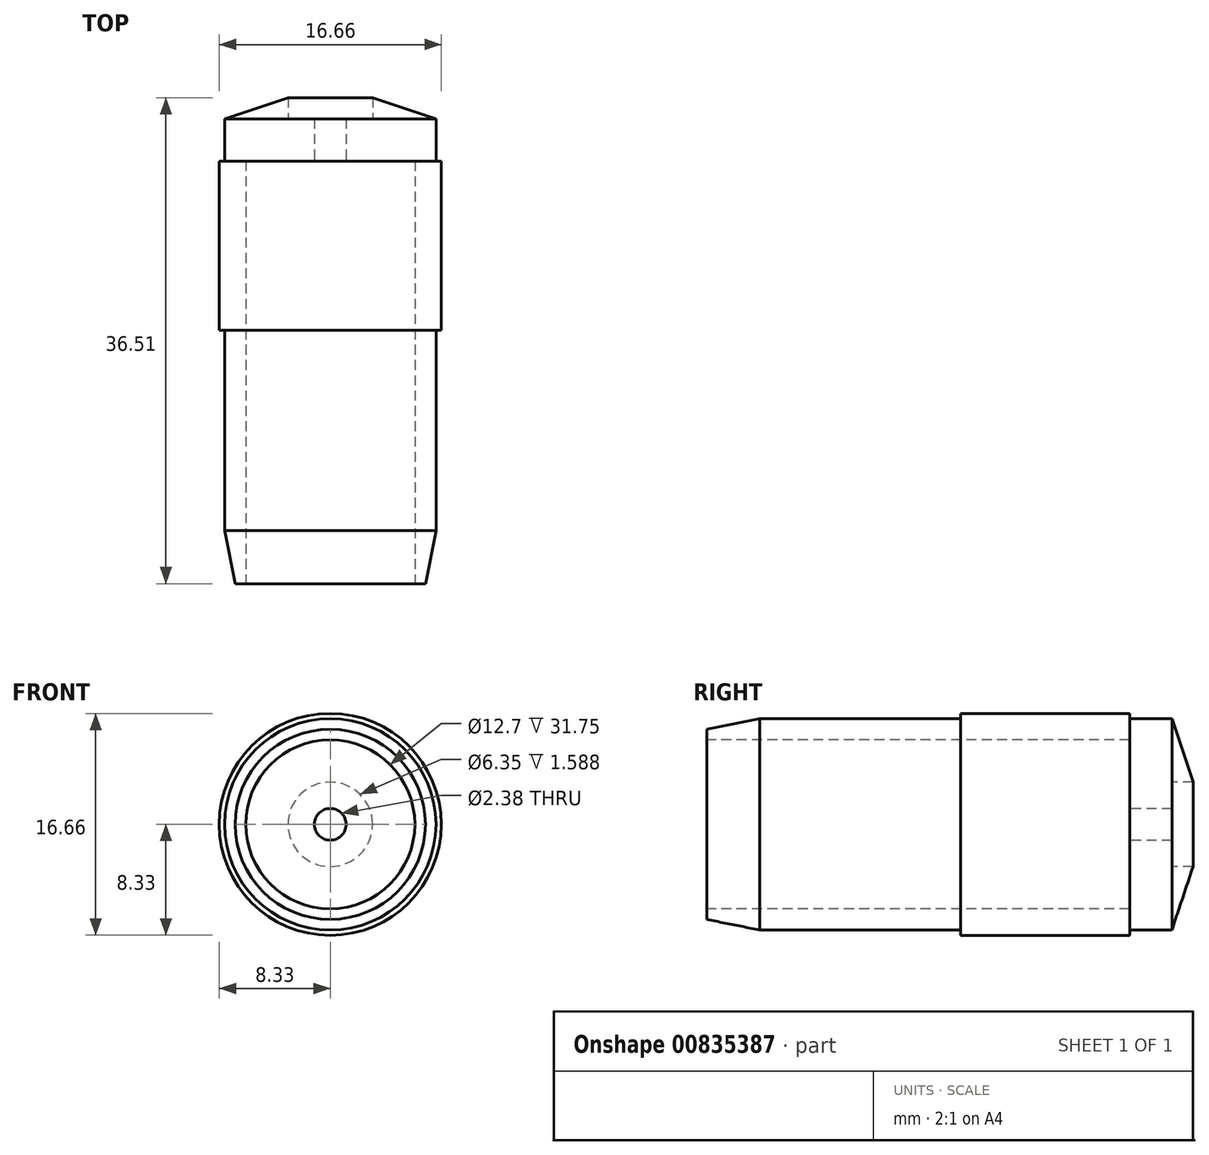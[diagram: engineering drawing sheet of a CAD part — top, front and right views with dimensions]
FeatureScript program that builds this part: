
annotation { "Feature Type Name" : "Feature", "Feature Type Description" : "" }
export const myFeature = defineFeature(function(context is Context, id is Id, definition is map)
    precondition{}
    {
        {
            var Q0;
            Q0=qCreatedBy(makeId("Top.planeOp"),FACE);
            var sketch = newSketch(context, id + "F0", { "sketchPlane" : qUnion([Q0])});
            skLineSegment(sketch, "E0", {"start": v(6.35, 0) * mm, "end": v(7.14, 0) * mm});
            skLineSegment(sketch, "E1", {"start": v(7.14, 0) * mm, "end": v(7.94, 4) * mm});
            skLineSegment(sketch, "E2", {"start": v(7.94, 4) * mm, "end": v(7.94, 19.05) * mm});
            skLineSegment(sketch, "E3", {"start": v(7.94, 19.05) * mm, "end": v(8.33, 19.05) * mm});
            skLineSegment(sketch, "E4", {"start": v(8.33, 19.05) * mm, "end": v(8.33, 31.75) * mm});
            skLineSegment(sketch, "E5", {"start": v(8.33, 31.75) * mm, "end": v(7.94, 31.75) * mm});
            skLineSegment(sketch, "E6", {"start": v(7.94, 31.75) * mm, "end": v(7.94, 34.93) * mm});
            skLineSegment(sketch, "E7", {"start": v(7.94, 34.93) * mm, "end": v(3.18, 36.51) * mm});
            skLineSegment(sketch, "E8", {"start": v(1.2, 31.75) * mm, "end": v(6.35, 31.75) * mm});
            skLineSegment(sketch, "E9", {"start": v(6.35, 31.75) * mm, "end": v(6.35, 0) * mm});
            skLineSegment(sketch, "E10", {"start": v(-6.35, 0) * mm, "end": v(-7.14, 0) * mm});
            skLineSegment(sketch, "E11", {"start": v(-7.14, 0) * mm, "end": v(-7.94, 4) * mm});
            skLineSegment(sketch, "E12", {"start": v(-7.94, 4) * mm, "end": v(-7.94, 19.05) * mm});
            skLineSegment(sketch, "E13", {"start": v(-7.94, 19.05) * mm, "end": v(-8.33, 19.05) * mm});
            skLineSegment(sketch, "E14", {"start": v(-8.33, 19.05) * mm, "end": v(-8.33, 31.75) * mm});
            skLineSegment(sketch, "E15", {"start": v(-8.33, 31.75) * mm, "end": v(-7.94, 31.75) * mm});
            skLineSegment(sketch, "E16", {"start": v(-7.94, 31.75) * mm, "end": v(-7.94, 34.93) * mm});
            skLineSegment(sketch, "E17", {"start": v(-7.94, 34.93) * mm, "end": v(-3.18, 36.51) * mm});
            skLineSegment(sketch, "E18", {"start": v(-1.2, 31.75) * mm, "end": v(-6.35, 31.75) * mm});
            skLineSegment(sketch, "E19", {"start": v(-6.35, 31.75) * mm, "end": v(-6.35, 0) * mm});
            skLineSegment(sketch, "E20", {"start": v(7.94, 4) * mm, "end": v(7.94, 0) * mm, "construction": true});
            skLineSegment(sketch, "E21", {"start": v(0, 0) * mm, "end": v(0, 36.51) * mm, "construction": true});
            skLineSegment(sketch, "E22", {"start": v(-3.18, 36.51) * mm, "end": v(-3.18, 34.92) * mm});
            skLineSegment(sketch, "E23", {"start": v(-3.18, 34.92) * mm, "end": v(-1.2, 34.92) * mm});
            skLineSegment(sketch, "E24", {"start": v(-1.2, 34.92) * mm, "end": v(-1.2, 31.75) * mm});
            skLineSegment(sketch, "E25", {"start": v(1.2, 31.75) * mm, "end": v(1.2, 34.92) * mm});
            skLineSegment(sketch, "E26", {"start": v(1.2, 34.92) * mm, "end": v(3.18, 34.92) * mm});
            skLineSegment(sketch, "E27", {"start": v(3.18, 34.92) * mm, "end": v(3.18, 36.51) * mm});
            skSolve(sketch);
        }
        {
            var Q0;
            Q0=makeQuery(id+"F0.imprint","IMPRINT",FACE,{"disambiguationData":[TD([[makeQuery(id+"F0.imprint","IMPRINT",EDGE,{"derivedFrom":sQuery(id+"F0.wireOp",EDGE,"E0")}),1.0]])]});
            var Q1;
            Q1=sQuery(id+"F0.wireOp",EDGE,"E21");
            revolve(context, id + "F1", {"surfaceOperationType" : NewSurfaceOperationType.NEW, "entities" : qUnion([Q0]), "axis" : qUnion([Q1]), "revolveType" : RevolveType.FULL});
        }
    });
